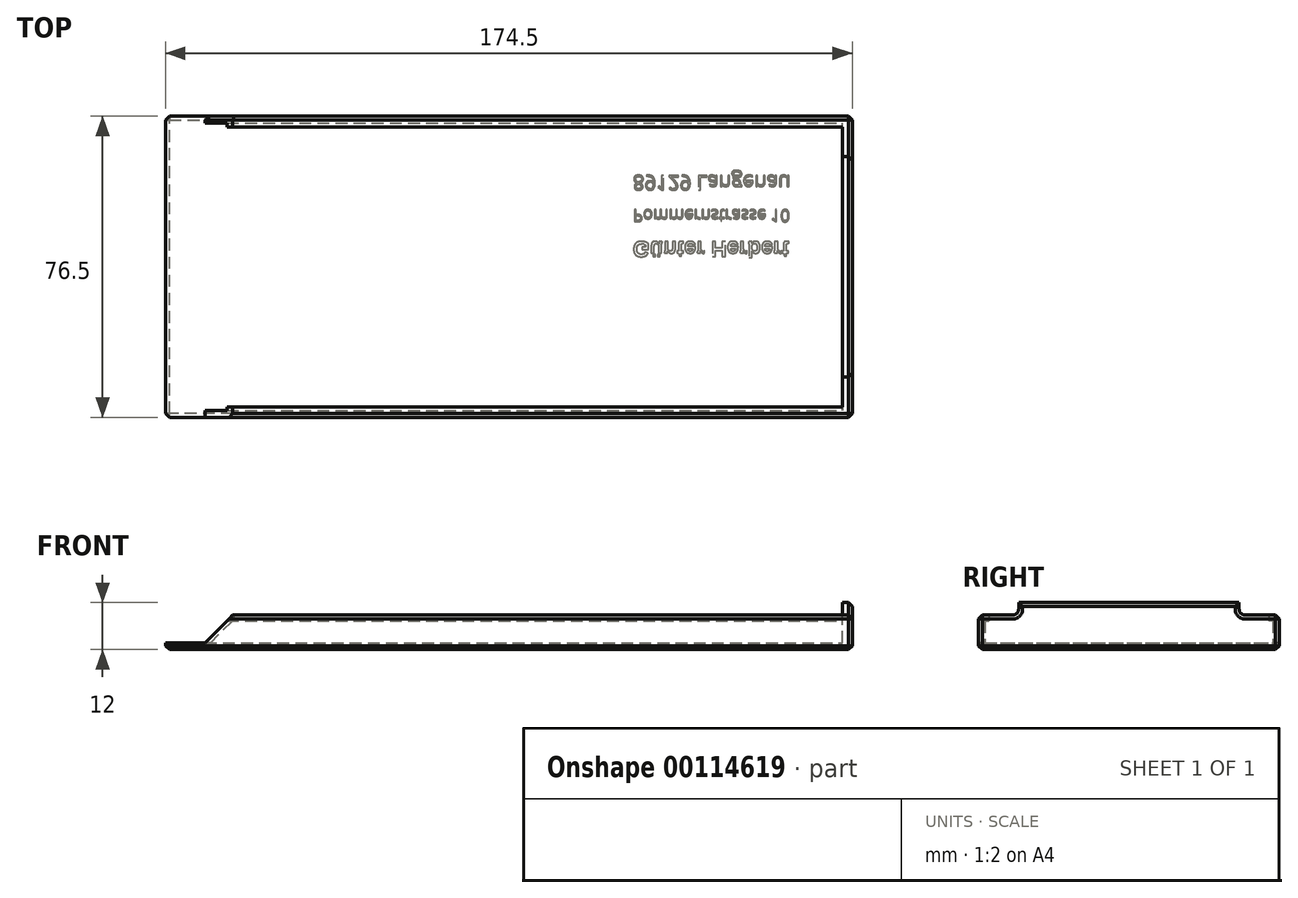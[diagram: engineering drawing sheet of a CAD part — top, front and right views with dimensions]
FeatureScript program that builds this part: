
annotation { "Feature Type Name" : "Feature", "Feature Type Description" : "" }
export const myFeature = defineFeature(function(context is Context, id is Id, definition is map)
    precondition{}
    {
        {
            var Q0;
            Q0=qCreatedBy(makeId("Right.planeOp"),FACE);
            var sketch = newSketch(context, id + "F0", { "sketchPlane" : qUnion([Q0])});
            skLineSegment(sketch, "E0", {"start": v(0, 0) * mm, "end": v(38.25, 0) * mm});
            skLineSegment(sketch, "E1", {"start": v(38.25, 0) * mm, "end": v(38.25, 8.8) * mm});
            skLineSegment(sketch, "E2", {"start": v(38.25, 8.8) * mm, "end": v(29.5, 8.8) * mm});
            skLineSegment(sketch, "E3", {"start": v(0, 12) * mm, "end": v(28, 12) * mm});
            skLineSegment(sketch, "E4", {"start": v(28, 12) * mm, "end": v(28, 10.3) * mm});
            skPoint(sketch, "E5.orphan", {"position": v(0, 8.8) * mm});
            skPoint(sketch, "E6.visualSharp", {"position": v(28, 8.8) * mm});
            skArc(sketch, "E6.filletArc", {"start": v(28, 10.3) * mm, "mid": v(28.44, 9.24) * mm, "end": v(29.5, 8.8) * mm});
            skLineSegment(sketch, "E7.MirrorCS", {"start": v(0, 0) * mm, "end": v(-38.25, 0) * mm});
            skLineSegment(sketch, "E8.MirrorCS", {"start": v(-38.25, 0) * mm, "end": v(-38.25, 8.8) * mm});
            skLineSegment(sketch, "E9.MirrorCS", {"start": v(-38.25, 8.8) * mm, "end": v(-29.5, 8.8) * mm});
            skArc(sketch, "E10.MirrorCS", {"start": v(-28, 10.3) * mm, "mid": v(-28.44, 9.24) * mm, "end": v(-29.5, 8.8) * mm});
            skLineSegment(sketch, "E11.MirrorCS", {"start": v(-28, 12) * mm, "end": v(-28, 10.3) * mm});
            skLineSegment(sketch, "E12.MirrorCS", {"start": v(0, 12) * mm, "end": v(-28, 12) * mm});
            skLineSegment(sketch, "E13.0", {"start": v(-36.55, 1.7) * mm, "end": v(-36.55, 7.3) * mm});
            skLineSegment(sketch, "E14.0", {"start": v(0, 1.7) * mm, "end": v(-36.55, 1.7) * mm});
            skLineSegment(sketch, "E15.0", {"start": v(0, 7.3) * mm, "end": v(-36.55, 7.3) * mm});
            skLineSegment(sketch, "E16.trimOffspring", {"start": v(-35.55, 7.3) * mm, "end": v(-35.55, 8.8) * mm});
            skLineSegment(sketch, "E17.MirrorCS", {"start": v(0, 7.3) * mm, "end": v(36.55, 7.3) * mm});
            skLineSegment(sketch, "E18.MirrorCS", {"start": v(35.55, 7.3) * mm, "end": v(35.55, 8.8) * mm});
            skLineSegment(sketch, "E19.MirrorCS", {"start": v(36.55, 1.7) * mm, "end": v(36.55, 7.3) * mm});
            skLineSegment(sketch, "E20.MirrorCS", {"start": v(0, 1.7) * mm, "end": v(36.55, 1.7) * mm});
            skSolve(sketch);
        }
        {
            var Q0;
            Q0=makeQuery(id+"F0.imprint","IMPRINT",FACE,{"disambiguationData":[TD([[makeQuery(id+"F0.imprint","IMPRINT",EDGE,{"derivedFrom":sQuery(id+"F0.wireOp",EDGE,"E0")}),1.0]])]});
            extrude(context, id + "F1", {"entities" : qUnion([Q0]), "oppositeDirection" : true, "depth" : (172) * mm});
        }
        {
            var Q0;
            Q0=makeQuery(id+"F0.imprint","IMPRINT",FACE,{"disambiguationData":[TD([[makeQuery(id+"F0.imprint","IMPRINT",EDGE,{"derivedFrom":sQuery(id+"F0.wireOp",EDGE,"E0")}),1.0]])]});
            var Q1;
            {var subQ1=sQuery(id+"F0.wireOp",EDGE,"E13.0");Q1=makeQuery(id+"F0.imprint","IMPRINT",FACE,{"disambiguationData":[TD([[makeQuery(id+"F0.imprint","IMPRINT",EDGE,{"derivedFrom":subQ1}),-1.0]])]});}
            var Q2;
            Q2=makeQuery(id+"F0.imprint","IMPRINT",FACE,{"disambiguationData":[TD([[makeQuery(id+"F0.imprint","IMPRINT",EDGE,{"derivedFrom":sQuery(id+"F0.wireOp",EDGE,"E3")}),-1.0]])]});
            extrude(context, id + "F2", {"entities" : qUnion([Q0, Q1, Q2]), "operationType" : NewBodyOperationType.ADD, "depth" : 2.5 * mm});
        }
        {
            var Q0;
            {var subQ0=sQuery(id+"F0.wireOp",EDGE,"E8.MirrorCS");Q0=makeQuery(id+"F2.boolean.opBoolean","MERGE",FACE,{"derivedFrom":[makeQuery(id+"F1.opExtrude","SWEPT_FACE",FACE,{"disambiguationData":[OSD([subQ0])]}),makeQuery(id+"F2.opExtrude","SWEPT_FACE",FACE,{"disambiguationData":[OSD([subQ0])]})]});}
            var sketch = newSketch(context, id + "F3", { "sketchPlane" : qUnion([Q0])});
            skLineSegment(sketch, "E21.0", {"start": v(-172, 1.7) * mm, "end": v(-162, 1.7) * mm});
            skLineSegment(sketch, "E22", {"start": v(-162, 1.7) * mm, "end": v(-154.9, 8.8) * mm});
            skLineSegment(sketch, "E23", {"start": v(-172, 8.8) * mm, "end": v(-172, 1.7) * mm});
            skLineSegment(sketch, "E24.0", {"start": v(-172, 8.8) * mm, "end": v(2.5, 8.8) * mm});
            skLineSegment(sketch, "E25", {"start": v(-154.9, 8.8) * mm, "end": v(-172, 8.8) * mm});
            skSolve(sketch);
        }
        {
            var Q0;
            {var subQ1=sQuery(id+"F3.wireOp",EDGE,"E21.0");Q0=makeQuery(id+"F3.imprint","IMPRINT",FACE,{"disambiguationData":[TD([[makeQuery(id+"F3.imprint","IMPRINT",EDGE,{"derivedFrom":subQ1}),1.0]])]});}
            extrude(context, id + "F4", {"entities" : qUnion([Q0]), "operationType" : NewBodyOperationType.REMOVE, "oppositeDirection" : true, "depth" : 100 * mm});
        }
        {
            var Q0;
            {var subQ0=sQuery(id+"F0.wireOp",EDGE,"E7.MirrorCS");var subQ1=sQuery(id+"F0.wireOp",EDGE,"E0");Q0=makeQuery(id+"F2.boolean.opBoolean","MERGE",FACE,{"derivedFrom":[makeQuery(id+"F1.opExtrude","SWEPT_FACE",FACE,{"disambiguationData":[OSD([subQ1,subQ0])]}),makeQuery(id+"F2.opExtrude","SWEPT_FACE",FACE,{"disambiguationData":[OSD([subQ1,subQ0])]})]});}
            var sketch = newSketch(context, id + "F5", { "sketchPlane" : qUnion([Q0])});
            skText(sketch, "E26", { "text": "Günter Herbert", "fontName": "Arimo-Bold.ttf"});
            skText(sketch, "E27", { "text": "Pommernstrasse 10", "fontName": "OpenSans-Regular.ttf"});
            skPoint(sketch, "E27.firstSnap0", {"position": v(-52.5, -4.42) * mm});
            skText(sketch, "E28", { "text": "89129 Langenau", "fontName": "OpenSans-Regular.ttf"});
            const initialGuessF5  = {"E26": [-0.0533, -0.00643, 1, 0, 0.00402], "E27": [-0.0533, -0.0145, 1, 0, 0.00307], "E28": [-0.0533, -0.02325, 1, 0, 0.00375]};
            skSetInitialGuess(sketch, initialGuessF5);
            skSolve(sketch);
        }
        {
            var Q0;
            Q0 = qSketchRegion(id + "F5", true);
            extrude(context, id + "F6", {"entities" : qUnion([Q0]), "operationType" : NewBodyOperationType.REMOVE, "oppositeDirection" : true, "depth" : 0.2 * mm});
        }
        {
            var Q0;
            Q0=makeQuery(id+"F2.opExtrude","CAP_EDGE",EDGE,{"disambiguationData":[OSD([sQuery(id+"F0.wireOp",EDGE,"E9.MirrorCS")])],"isStart":false});
            var Q1;
            Q1=makeQuery(id+"F2.opExtrude","CAP_EDGE",EDGE,{"disambiguationData":[OSD([sQuery(id+"F0.wireOp",EDGE,"E8.MirrorCS")])],"isStart":false});
            var Q2;
            {var subQ0=sQuery(id+"F0.wireOp",EDGE,"E9.MirrorCS");var subQ1=sQuery(id+"F0.wireOp",EDGE,"E8.MirrorCS");Q2=makeQuery(id+"F2.boolean.opBoolean","MERGE",EDGE,{"derivedFrom":[makeQuery(id+"F1.opExtrude","SWEPT_EDGE",EDGE,{"disambiguationData":[OSD([subQ1,subQ0])]}),makeQuery(id+"F2.opExtrude","SWEPT_EDGE",EDGE,{"disambiguationData":[OSD([subQ1,subQ0])]})]});}
            var Q3;
            Q3=makeQuery(id+"F2.opExtrude","CAP_EDGE",EDGE,{"disambiguationData":[OSD([sQuery(id+"F0.wireOp",EDGE,"E3"),sQuery(id+"F0.wireOp",EDGE,"E12.MirrorCS")])],"isStart":false});
            var Q4;
            Q4=makeQuery(id+"F2.opExtrude","CAP_EDGE",EDGE,{"disambiguationData":[OSD([sQuery(id+"F0.wireOp",EDGE,"E10.MirrorCS")])],"isStart":false});
            var Q5;
            Q5=makeQuery(id+"F2.opExtrude","CAP_EDGE",EDGE,{"disambiguationData":[OSD([sQuery(id+"F0.wireOp",EDGE,"E11.MirrorCS")])],"isStart":false});
            var Q6;
            {var subQ0=sQuery(id+"F0.wireOp",EDGE,"E8.MirrorCS");var subQ1=sQuery(id+"F0.wireOp",EDGE,"E7.MirrorCS");Q6=makeQuery(id+"F2.boolean.opBoolean","MERGE",EDGE,{"derivedFrom":[makeQuery(id+"F1.opExtrude","SWEPT_EDGE",EDGE,{"disambiguationData":[OSD([subQ1,subQ0])]}),makeQuery(id+"F2.opExtrude","SWEPT_EDGE",EDGE,{"disambiguationData":[OSD([subQ1,subQ0])]})]});}
            var Q7;
            Q7=makeQuery(id+"F4.boolean.opBoolean","COPY",EDGE,{"derivedFrom":makeQuery(id+"F4.opExtrude","CAP_EDGE",EDGE,{"disambiguationData":[OSD([sQuery(id+"F3.wireOp",EDGE,"E22")])],"isStart":true})});
            var Q8;
            Q8=makeQuery(id+"F2.opExtrude","CAP_EDGE",EDGE,{"disambiguationData":[OSD([sQuery(id+"F0.wireOp",EDGE,"E4")])],"isStart":false});
            var Q9;
            Q9=makeQuery(id+"F2.opExtrude","CAP_EDGE",EDGE,{"disambiguationData":[OSD([sQuery(id+"F0.wireOp",EDGE,"E6.filletArc")])],"isStart":false});
            var Q10;
            Q10=makeQuery(id+"F2.opExtrude","CAP_EDGE",EDGE,{"disambiguationData":[OSD([sQuery(id+"F0.wireOp",EDGE,"E2")])],"isStart":false});
            var Q11;
            {var subQ0=sQuery(id+"F0.wireOp",EDGE,"E1");Q11=makeQuery(id+"F4.boolean.opBoolean","INTERSECT",EDGE,{"derivedFrom":[makeQuery(id+"F2.boolean.opBoolean","MERGE",FACE,{"derivedFrom":[makeQuery(id+"F1.opExtrude","SWEPT_FACE",FACE,{"disambiguationData":[OSD([subQ0])]}),makeQuery(id+"F2.opExtrude","SWEPT_FACE",FACE,{"disambiguationData":[OSD([subQ0])]})]}),makeQuery(id+"F4.opExtrude","SWEPT_FACE",FACE,{"disambiguationData":[OSD([sQuery(id+"F3.wireOp",EDGE,"E22")])]})]});}
            var Q12;
            {var subQ0=sQuery(id+"F0.wireOp",EDGE,"E1");var subQ1=sQuery(id+"F0.wireOp",EDGE,"E0");Q12=makeQuery(id+"F2.boolean.opBoolean","MERGE",EDGE,{"derivedFrom":[makeQuery(id+"F1.opExtrude","SWEPT_EDGE",EDGE,{"disambiguationData":[OSD([subQ1,subQ0])]}),makeQuery(id+"F2.opExtrude","SWEPT_EDGE",EDGE,{"disambiguationData":[OSD([subQ1,subQ0])]})]});}
            var Q13;
            Q13=makeQuery(id+"F1.opExtrude","CAP_EDGE",EDGE,{"disambiguationData":[OSD([sQuery(id+"F0.wireOp",EDGE,"E0"),sQuery(id+"F0.wireOp",EDGE,"E7.MirrorCS")])],"isStart":false});
            var Q14;
            Q14=makeQuery(id+"F2.opExtrude","CAP_EDGE",EDGE,{"disambiguationData":[OSD([sQuery(id+"F0.wireOp",EDGE,"E0"),sQuery(id+"F0.wireOp",EDGE,"E7.MirrorCS")])],"isStart":false});
            var Q15;
            Q15=makeQuery(id+"F1.opExtrude","CAP_EDGE",EDGE,{"disambiguationData":[OSD([sQuery(id+"F0.wireOp",EDGE,"E1")])],"isStart":false});
            var Q16;
            Q16=makeQuery(id+"F1.opExtrude","CAP_EDGE",EDGE,{"disambiguationData":[OSD([sQuery(id+"F0.wireOp",EDGE,"E8.MirrorCS")])],"isStart":false});
            var Q17;
            Q17=makeQuery(id+"F2.opExtrude","CAP_EDGE",EDGE,{"disambiguationData":[OSD([sQuery(id+"F0.wireOp",EDGE,"E1")])],"isStart":false});
            var Q18;
            {var subQ0=sQuery(id+"F0.wireOp",EDGE,"E2");var subQ1=sQuery(id+"F0.wireOp",EDGE,"E1");Q18=makeQuery(id+"F2.boolean.opBoolean","MERGE",EDGE,{"derivedFrom":[makeQuery(id+"F1.opExtrude","SWEPT_EDGE",EDGE,{"disambiguationData":[OSD([subQ1,subQ0])]}),makeQuery(id+"F2.opExtrude","SWEPT_EDGE",EDGE,{"disambiguationData":[OSD([subQ1,subQ0])]})]});}
            chamfer(context, id + "F7", {"entities" : qUnion([Q0, Q1, Q2, Q3, Q4, Q5, Q6, Q7, Q8, Q9, Q10, Q11, Q12, Q13, Q14, Q15, Q16, Q17, Q18]), "width" : 1 * mm, "tangentPropagation" : true});
        }
    });
